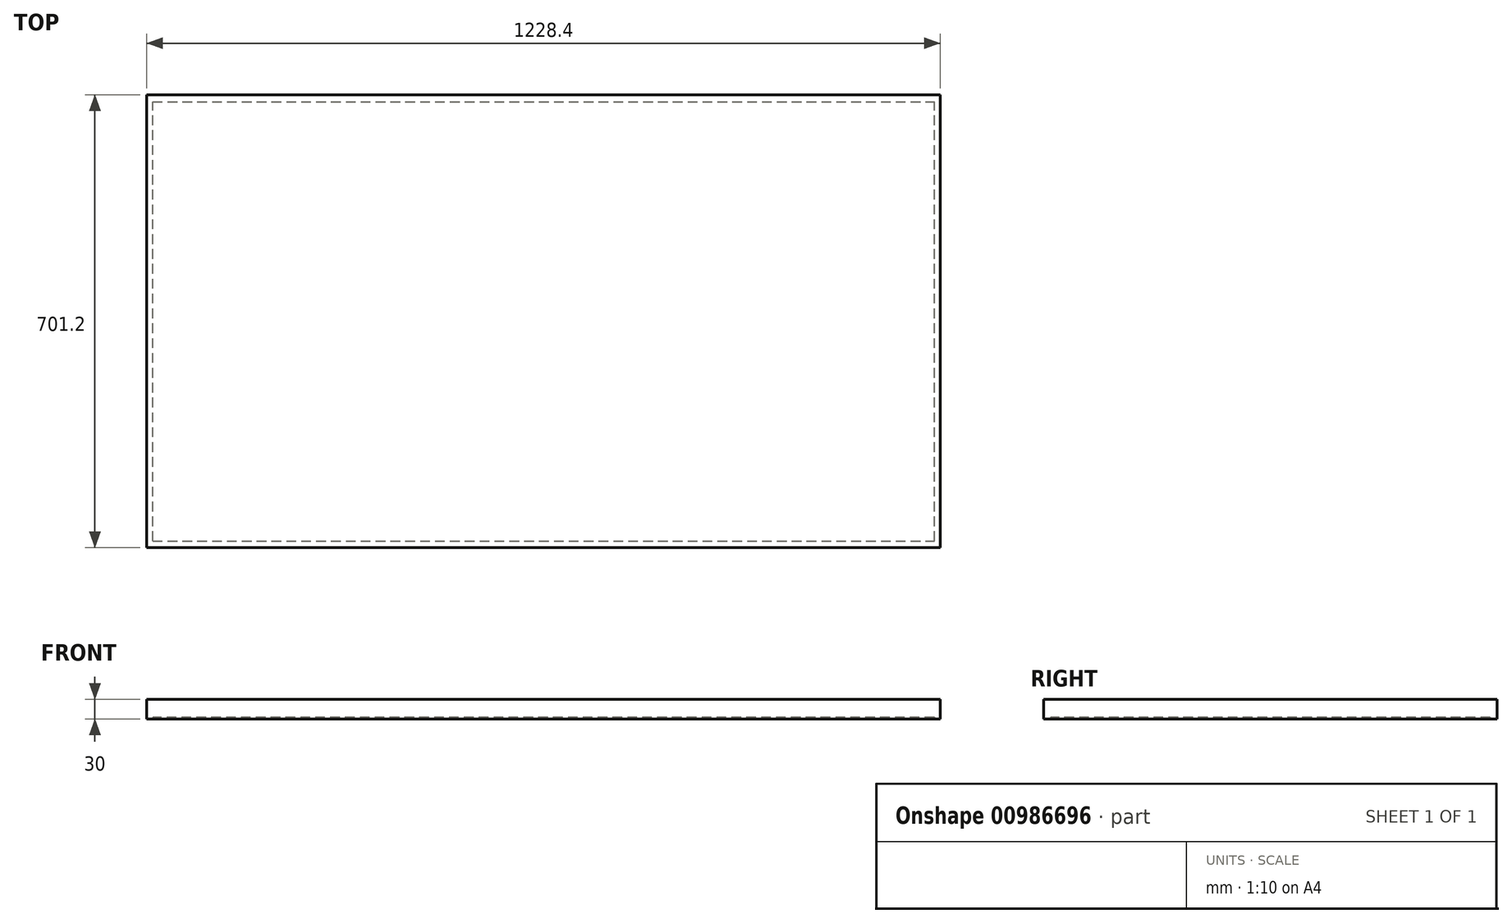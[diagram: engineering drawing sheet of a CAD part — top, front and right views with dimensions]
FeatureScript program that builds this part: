
annotation { "Feature Type Name" : "Feature", "Feature Type Description" : "" }
export const myFeature = defineFeature(function(context is Context, id is Id, definition is map)
    precondition{}
    {
        {
            var Q0;
            Q0=qCreatedBy(makeId("Top.planeOp"),FACE);
            var sketch = newSketch(context, id + "F0", { "sketchPlane" : qUnion([Q0])});
            skLineSegment(sketch, "E0.bottom", {"start": v(614.2, 350.6) * mm, "end": v(-614.2, 350.6) * mm});
            skLineSegment(sketch, "E0.top", {"start": v(614.2, -350.6) * mm, "end": v(-614.2, -350.6) * mm});
            skLineSegment(sketch, "E0.left", {"start": v(614.2, 350.6) * mm, "end": v(614.2, -350.6) * mm});
            skLineSegment(sketch, "E0.right", {"start": v(-614.2, 350.6) * mm, "end": v(-614.2, -350.6) * mm});
            skPoint(sketch, "E0.middle", {"position": v(0, 0) * mm});
            skSolve(sketch);
        }
        {
            var Q0;
            Q0=makeQuery(id+"F0.imprint","IMPRINT",FACE,{"disambiguationData":[TD([[makeQuery(id+"F0.imprint","IMPRINT",EDGE,{"derivedFrom":sQuery(id+"F0.wireOp",EDGE,"E0.bottom")}),1.0]])]});
            extrude(context, id + "F1", {"entities" : qUnion([Q0]), "depth" : 30 * mm, "offsetDistance" : 25 * mm});
        }
        {
            var Q0;
            Q0=makeQuery(id+"F1.opExtrude","CAP_FACE",FACE,{"disambiguationData":[OSD([sQuery(id+"F0.wireOp",EDGE,"E0.bottom"),sQuery(id+"F0.wireOp",EDGE,"E0.top"),sQuery(id+"F0.wireOp",EDGE,"E0.left"),sQuery(id+"F0.wireOp",EDGE,"E0.right")])],"isStart":true});
            var sketch = newSketch(context, id + "F2", { "sketchPlane" : qUnion([Q0])});
            skLineSegment(sketch, "E1.bottom", {"start": v(604.8, -340.2) * mm, "end": v(-604.8, -340.2) * mm});
            skLineSegment(sketch, "E1.top", {"start": v(604.8, 340.2) * mm, "end": v(-604.8, 340.2) * mm});
            skLineSegment(sketch, "E1.left", {"start": v(604.8, -340.2) * mm, "end": v(604.8, 340.2) * mm});
            skLineSegment(sketch, "E1.right", {"start": v(-604.8, -340.2) * mm, "end": v(-604.8, 340.2) * mm});
            skPoint(sketch, "E1.middle", {"position": v(0, 0) * mm});
            skSolve(sketch);
        }
        {
            var Q0;
            Q0=makeQuery(id+"F2.imprint","IMPRINT",FACE,{"disambiguationData":[TD([[makeQuery(id+"F2.imprint","IMPRINT",EDGE,{"derivedFrom":sQuery(id+"F2.wireOp",EDGE,"E1.bottom")}),-1.0]])]});
            extrude(context, id + "F3", {"entities" : qUnion([Q0]), "operationType" : NewBodyOperationType.REMOVE, "endBound" : BoundingType.SYMMETRIC, "oppositeDirection" : true, "depth" : -5 * mm, "offsetDistance" : -5 * mm});
        }
    });
